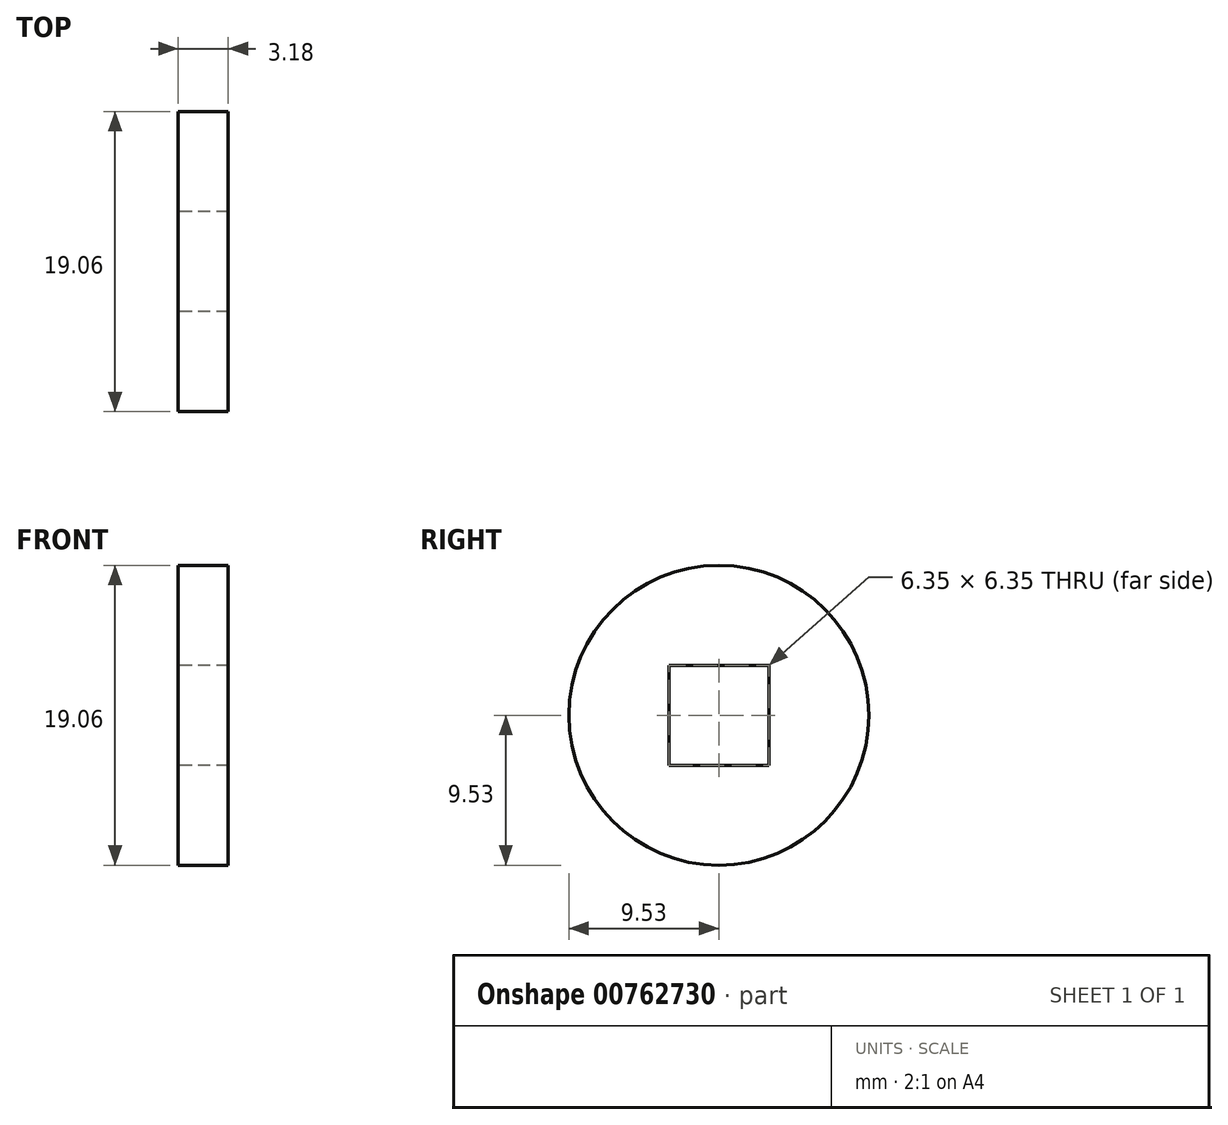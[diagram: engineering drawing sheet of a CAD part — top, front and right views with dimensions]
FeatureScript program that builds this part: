
annotation { "Feature Type Name" : "Feature", "Feature Type Description" : "" }
export const myFeature = defineFeature(function(context is Context, id is Id, definition is map)
    precondition{}
    {
        {
            var Q0;
            Q0=qCreatedBy(makeId("Right.planeOp"),FACE);
            var sketch = newSketch(context, id + "F0", { "sketchPlane" : qUnion([Q0])});
            skCircle(sketch, "E0", {"center": v(0, 0) * mm, "radius": 9.53 * mm});
            skLineSegment(sketch, "E1", {"start": v(-3.17, 3.17) * mm, "end": v(3.17, 3.17) * mm});
            skLineSegment(sketch, "E2", {"start": v(3.18, 3.17) * mm, "end": v(3.18, -3.17) * mm});
            skLineSegment(sketch, "E3", {"start": v(3.18, -3.17) * mm, "end": v(-3.17, -3.18) * mm});
            skLineSegment(sketch, "E4", {"start": v(-3.17, 3.18) * mm, "end": v(-3.18, -3.17) * mm});
            skSolve(sketch);
        }
        {
            var Q0;
            Q0=makeQuery(id+"F0.imprint","IMPRINT",FACE,{"disambiguationData":[TD([[makeQuery(id+"F0.imprint","IMPRINT",EDGE,{"derivedFrom":sQuery(id+"F0.wireOp",EDGE,"E0")}),1.0]])]});
            extrude(context, id + "F1", {"entities" : qUnion([Q0]), "depth" : 3.17 * mm, "offsetDistance" : 25.4 * mm});
        }
    });
